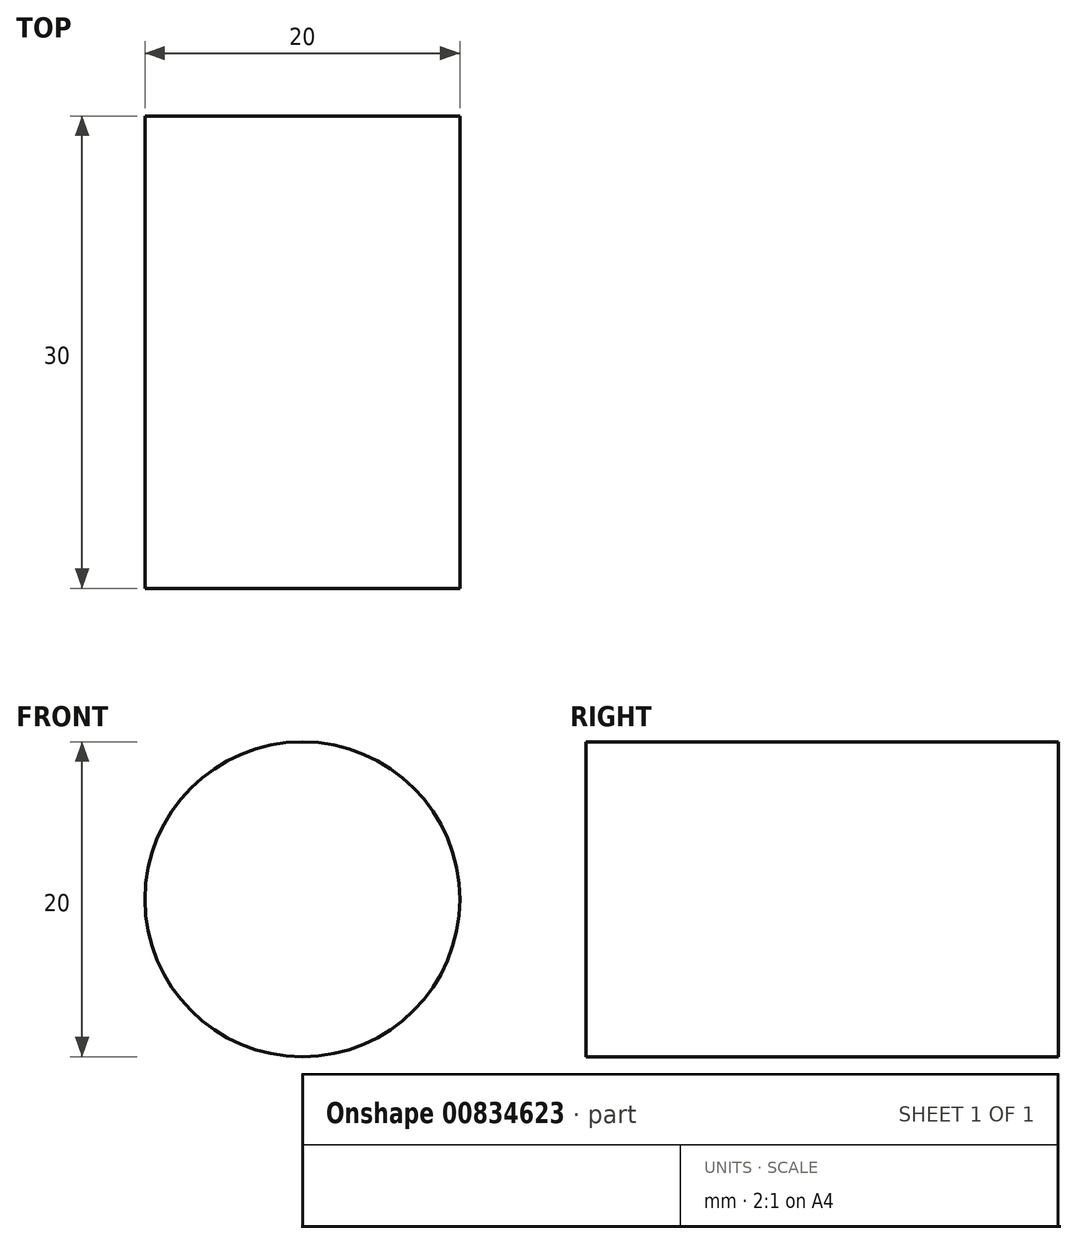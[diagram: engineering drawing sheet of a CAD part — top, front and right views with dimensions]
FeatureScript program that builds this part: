
annotation { "Feature Type Name" : "Feature", "Feature Type Description" : "" }
export const myFeature = defineFeature(function(context is Context, id is Id, definition is map)
    precondition{}
    {
        {
            var Q0;
            Q0=qCreatedBy(makeId("Front.planeOp"),FACE);
            var sketch = newSketch(context, id + "F0", { "sketchPlane" : qUnion([Q0])});
            skCircle(sketch, "E0", {"center": v(-44.5, -39.93) * mm, "radius": 10 * mm});
            skSolve(sketch);
        }
        {
            var Q0;
            Q0 = qSketchRegion(id + "F0", true);
            extrude(context, id + "F1", {"entities" : qUnion([Q0]), "depth" : 30 * mm, "offsetDistance" : 25 * mm});
        }
    });
